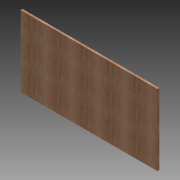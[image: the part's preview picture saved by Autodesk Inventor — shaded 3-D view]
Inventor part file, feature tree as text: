
AUTODESK INVENTOR PART (.ipt)
format: ipt  version: 2013 (Build 170138000, 138)  size: 88,576 bytes
history: native  units: in
note: dims shown in document units (in); Inventor stores cm internally (conversion verified against a paired STEP export)
features: extrude x1, sketch x1
ambient origin geometry x8: Origin, YZ Plane, XZ Plane, XY Plane, X Axis, Y Axis, Z Axis, Center Point
bodies: Solid1 (feature_tree)
feature tree (2):
  extrude  "Extrusion1"  Depth=27.0in
  sketch  "Sketch1"  dims[d0=52.0in d1=27.0in d2=0.75in d3=0.0in]
